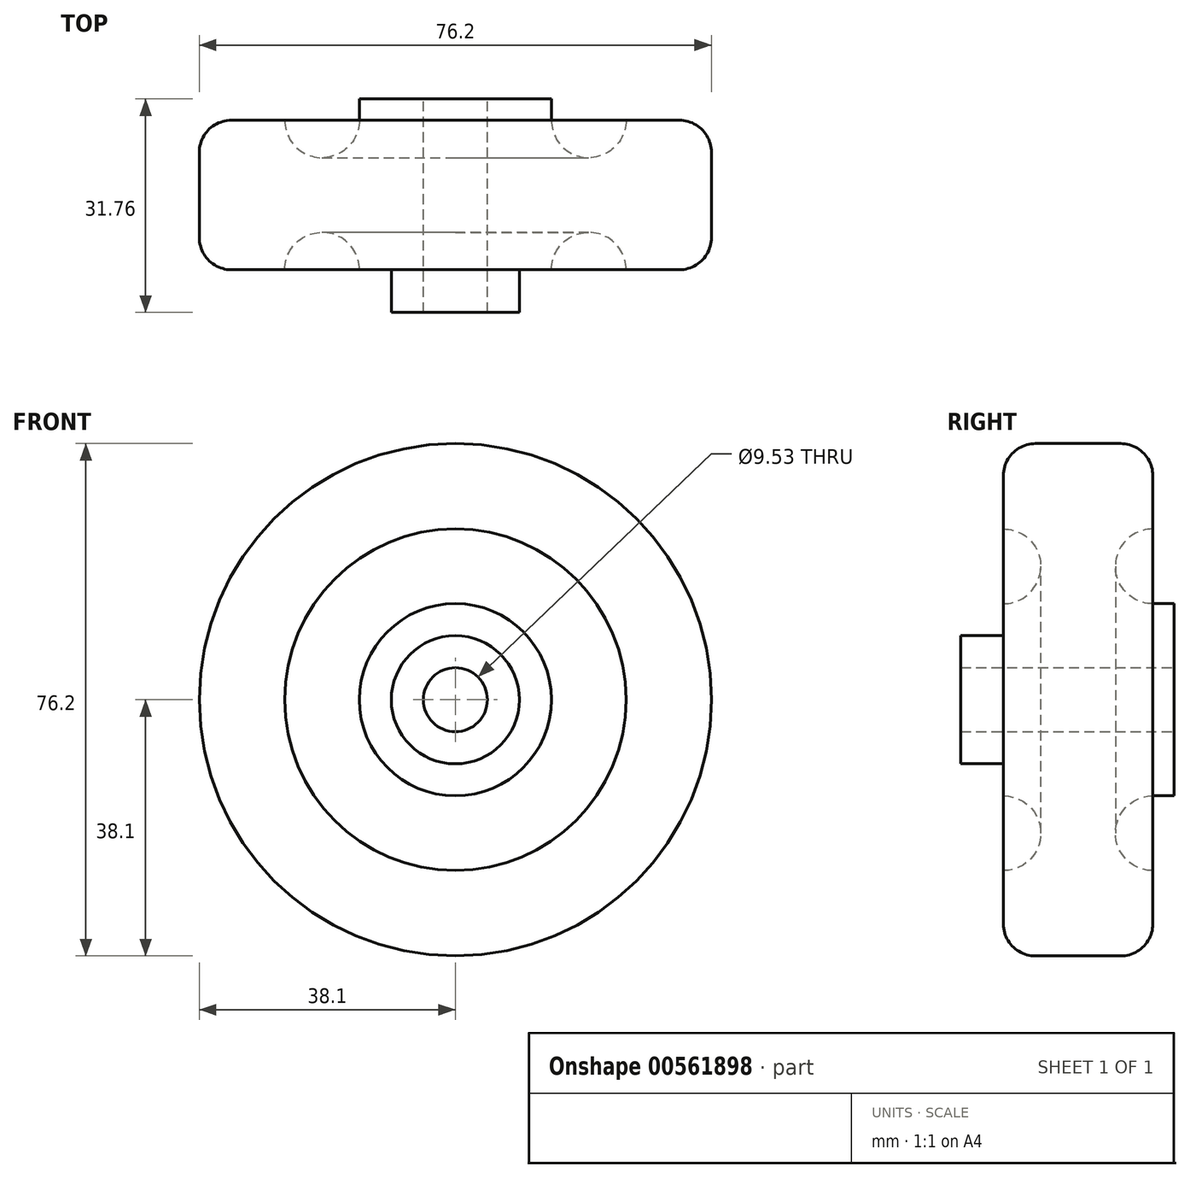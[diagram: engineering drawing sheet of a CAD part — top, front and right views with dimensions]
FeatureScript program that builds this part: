
annotation { "Feature Type Name" : "Feature", "Feature Type Description" : "" }
export const myFeature = defineFeature(function(context is Context, id is Id, definition is map)
    precondition{}
    {
        {
            var Q0;
            Q0=qCreatedBy(makeId("Front.planeOp"),FACE);
            var sketch = newSketch(context, id + "F0", { "sketchPlane" : qUnion([Q0])});
            skCircle(sketch, "E0", {"center": v(0, 0) * mm, "radius": 38.1 * mm});
            skSolve(sketch);
        }
        {
            var Q0;
            Q0=makeQuery(id+"F0.imprint","IMPRINT",FACE,{"disambiguationData":[TD([[makeQuery(id+"F0.imprint","IMPRINT",EDGE,{"derivedFrom":sQuery(id+"F0.wireOp",EDGE,"E0")}),1.0]])]});
            extrude(context, id + "F1", {"entities" : qUnion([Q0]), "depth" : 22.22 * mm});
        }
        {
            var Q0;
            Q0=sQuery(id+"F0.wireOp",VERTEX,"E0.center");
            var Q1;
            Q1=makeQuery(id+"F1.opExtrude","SWEPT_BODY",BODY,{"disambiguationData":[OSD([sQuery(id+"F0.wireOp",EDGE,"E0")])]});
            hole(context, id + "F2", {"style" : HoleStyle.SIMPLE, "endStyle" : HoleEndStyle.THROUGH, "oppositeDirection" : true, "holeDiameter" : 9.52 * mm, "isTappedThrough" : true, "tappedDepth" : 12.7 * mm, "tapClearance" : 3, "startFromSketch" : true, "locations" : qUnion([Q0]), "scope" : qUnion([Q1])});
        }
        {
            var Q0;
            Q0=makeQuery(id+"F1.opExtrude","CAP_FACE",FACE,{"disambiguationData":[OSD([sQuery(id+"F0.wireOp",EDGE,"E0")])],"isStart":false});
            var sketch = newSketch(context, id + "F3", { "sketchPlane" : qUnion([Q0])});
            skCircle(sketch, "E1", {"center": v(0, 0) * mm, "radius": 9.53 * mm});
            skSolve(sketch);
        }
        {
            var Q0;
            Q0=makeQuery(id+"F3.imprint","IMPRINT",FACE,{"disambiguationData":[TD([[makeQuery(id+"F3.imprint","IMPRINT",EDGE,{"derivedFrom":sQuery(id+"F3.wireOp",EDGE,"E1")}),1.0]])]});
            extrude(context, id + "F4", {"entities" : qUnion([Q0]), "operationType" : NewBodyOperationType.ADD, "depth" : 6.35 * mm, "offsetDistance" : 25.4 * mm});
        }
        {
            var Q0;
            Q0=makeQuery(id+"F0.imprint","IMPRINT",FACE,{"disambiguationData":[TD([[makeQuery(id+"F0.imprint","IMPRINT",EDGE,{"derivedFrom":sQuery(id+"F0.wireOp",EDGE,"E0")}),1.0]])]});
            var sketch = newSketch(context, id + "F5", { "sketchPlane" : qUnion([Q0])});
            skCircle(sketch, "E2", {"center": v(0, 0) * mm, "radius": 14.29 * mm});
            skCircle(sketch, "E3.0", {"center": v(0, 0) * mm, "radius": 4.76 * mm});
            skSolve(sketch);
        }
        {
            var Q0;
            Q0=qSketchRegion(id+"F5",true);
            extrude(context, id + "F6", {"entities" : qUnion([Q0]), "operationType" : NewBodyOperationType.ADD, "oppositeDirection" : true, "depth" : 3.17 * mm});
        }
        {
            var Q0;
            Q0=makeQuery(id+"F1.opExtrude","CAP_EDGE",EDGE,{"disambiguationData":[OSD([sQuery(id+"F0.wireOp",EDGE,"E0")])],"isStart":true});
            var Q1;
            Q1=makeQuery(id+"F1.opExtrude","CAP_EDGE",EDGE,{"disambiguationData":[OSD([sQuery(id+"F0.wireOp",EDGE,"E0")])],"isStart":false});
            fillet(context, id + "F7", {"entities" : qUnion([Q0, Q1]), "radius" : 4.76 * mm, "tangentPropagation" : true, "allowEdgeOverflow" : false});
        }
        {
            var Q0;
            Q0=qCreatedBy(makeId("Right.planeOp"),FACE);
            var sketch = newSketch(context, id + "F8", { "sketchPlane" : qUnion([Q0])});
            skLineSegment(sketch, "E4.0", {"start": v(0, -14.29) * mm, "end": v(0, 14.29) * mm, "construction": true});
            skLineSegment(sketch, "E5.0", {"start": v(0, -14.29) * mm, "end": v(0, 14.29) * mm});
            skLineSegment(sketch, "E6.0", {"start": v(0, 33.34) * mm, "end": v(0, -33.34) * mm, "construction": true});
            skCircle(sketch, "E7", {"center": v(0, 19.84) * mm, "radius": 5.56 * mm});
            skPoint(sketch, "E8.0", {"position": v(0, 0) * mm});
            skLineSegment(sketch, "E9.0.0", {"start": v(-22.23, -33.34) * mm, "end": v(-22.23, 33.34) * mm, "construction": true});
            skCircle(sketch, "E10", {"center": v(-22.23, 19.84) * mm, "radius": 5.56 * mm});
            skPoint(sketch, "E11", {"position": v(-22.23, 0) * mm});
            skSolve(sketch);
        }
        {
            var Q0;
            Q0=makeQuery(id+"F8.imprint","IMPRINT",FACE,{"disambiguationData":[TD([[makeQuery(id+"F8.imprint","IMPRINT",EDGE,{"derivedFrom":sQuery(id+"F8.wireOp",EDGE,"E7")}),1.0]])]});
            var Q1;
            Q1=sQuery(id+"F8.wireOp",EDGE,"E7");
            var Q2;
            {var subQ0=sQuery(id+"F2.hole-0.sketch.wireOp",EDGE,"core_line_2");Q2=makeQuery(id+"F6.boolean.opBoolean","MERGE",FACE,{"derivedFrom":[makeQuery(id+"F4.boolean.opBoolean","MERGE",FACE,{"derivedFrom":[makeQuery(id+"F2.hole-0.boolean.opBoolean","COPY",FACE,{"derivedFrom":makeQuery(id+"F2.hole-0.opRevolve","SWEPT_FACE",FACE,{"disambiguationData":[OSD([subQ0])]})}),makeQuery(id+"F4.opExtrude","SWEPT_FACE",FACE,{"disambiguationData":[OSD([sQuery(id+"F0.wireOp",EDGE,"E0"),subQ0])]})]}),makeQuery(id+"F6.opExtrude","SWEPT_FACE",FACE,{"disambiguationData":[OSD([sQuery(id+"F5.wireOp",EDGE,"E3.0")])]})]});}
            revolve(context, id + "F9", {"operationType" : NewBodyOperationType.REMOVE, "entities" : qUnion([Q0]), "surfaceEntities" : qUnion([Q1]), "axis" : qUnion([Q2]), "revolveType" : RevolveType.FULL, "oppositeDirection" : true});
        }
        {
            var Q0;
            Q0=makeQuery(id+"F8.imprint","IMPRINT",FACE,{"disambiguationData":[TD([[makeQuery(id+"F8.imprint","IMPRINT",EDGE,{"derivedFrom":sQuery(id+"F8.wireOp",EDGE,"E10")}),1.0]])]});
            var Q1;
            Q1=sQuery(id+"F8.wireOp",EDGE,"E10");
            var Q2;
            {var subQ0=sQuery(id+"F2.hole-0.sketch.wireOp",EDGE,"core_line_2");Q2=makeQuery(id+"F6.boolean.opBoolean","MERGE",FACE,{"derivedFrom":[makeQuery(id+"F4.boolean.opBoolean","MERGE",FACE,{"derivedFrom":[makeQuery(id+"F2.hole-0.boolean.opBoolean","COPY",FACE,{"derivedFrom":makeQuery(id+"F2.hole-0.opRevolve","SWEPT_FACE",FACE,{"disambiguationData":[OSD([subQ0])]})}),makeQuery(id+"F4.opExtrude","SWEPT_FACE",FACE,{"disambiguationData":[OSD([sQuery(id+"F0.wireOp",EDGE,"E0"),subQ0])]})]}),makeQuery(id+"F6.opExtrude","SWEPT_FACE",FACE,{"disambiguationData":[OSD([sQuery(id+"F5.wireOp",EDGE,"E3.0")])]})]});}
            revolve(context, id + "F10", {"operationType" : NewBodyOperationType.REMOVE, "entities" : qUnion([Q0]), "surfaceEntities" : qUnion([Q1]), "axis" : qUnion([Q2]), "revolveType" : RevolveType.FULL, "oppositeDirection" : true});
        }
    });
